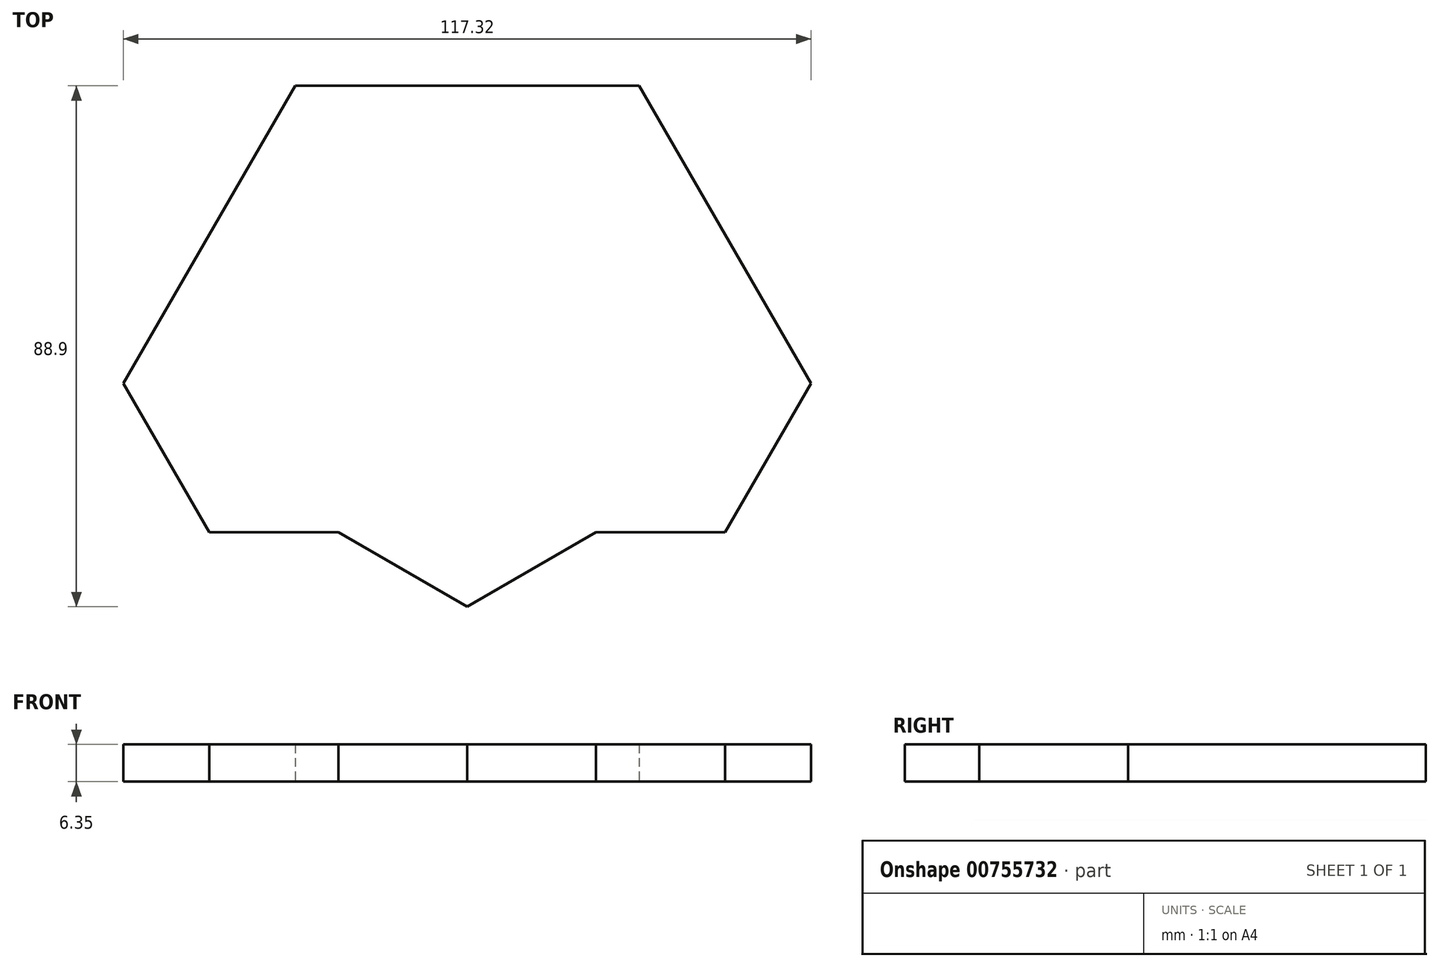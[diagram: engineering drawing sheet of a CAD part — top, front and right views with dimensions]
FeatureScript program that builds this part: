
annotation { "Feature Type Name" : "Feature", "Feature Type Description" : "" }
export const myFeature = defineFeature(function(context is Context, id is Id, definition is map)
    precondition{}
    {
        {
            var Q0;
            Q0=qCreatedBy(makeId("Top.planeOp"),FACE);
            var sketch = newSketch(context, id + "F0", { "sketchPlane" : qUnion([Q0])});
            skLineSegment(sketch, "E0.bottom", {"start": v(-63.5, 50.8) * mm, "end": v(63.5, 50.8) * mm});
            skLineSegment(sketch, "E0.top", {"start": v(-63.5, -50.8) * mm, "end": v(63.5, -50.8) * mm});
            skLineSegment(sketch, "E0.left", {"start": v(-63.5, 50.8) * mm, "end": v(-63.5, -50.8) * mm});
            skLineSegment(sketch, "E0.right", {"start": v(63.5, 50.8) * mm, "end": v(63.5, -50.8) * mm});
            skPoint(sketch, "E0.middle", {"position": v(0, 0) * mm});
            skCircle(sketch, "E1.cCircle", {"center": v(0, 0) * mm, "radius": 50.8 * mm, "construction": true});
            skLineSegment(sketch, "E1.0", {"start": v(-29.33, 50.8) * mm, "end": v(29.33, 50.8) * mm});
            skLineSegment(sketch, "E1.1", {"start": v(29.33, 50.8) * mm, "end": v(58.66, 0) * mm});
            skLineSegment(sketch, "E1.2", {"start": v(58.66, 0) * mm, "end": v(29.33, -50.8) * mm});
            skLineSegment(sketch, "E1.3", {"start": v(29.33, -50.8) * mm, "end": v(-29.33, -50.8) * mm});
            skLineSegment(sketch, "E1.4", {"start": v(-29.33, -50.8) * mm, "end": v(-58.66, 0) * mm});
            skLineSegment(sketch, "E1.5", {"start": v(-58.66, 0) * mm, "end": v(-29.33, 50.8) * mm});
            skPoint(sketch, "E1.0.midPoint", {"position": v(0, 50.8) * mm});
            skLineSegment(sketch, "E2", {"start": v(-44, 25.4) * mm, "end": v(44, 25.4) * mm});
            skLineSegment(sketch, "E3", {"start": v(44, 25.4) * mm, "end": v(44, -25.4) * mm});
            skLineSegment(sketch, "E4", {"start": v(44, -25.4) * mm, "end": v(-44, -25.4) * mm});
            skLineSegment(sketch, "E5", {"start": v(-44, -25.4) * mm, "end": v(-44, 25.4) * mm});
            skLineSegment(sketch, "E6", {"start": v(0, 25.4) * mm, "end": v(0, 50.8) * mm});
            skLineSegment(sketch, "E7", {"start": v(-44, 25.4) * mm, "end": v(0, 25.4) * mm});
            skLineSegment(sketch, "E8", {"start": v(-22, 25.4) * mm, "end": v(0, 38.1) * mm});
            skLineSegment(sketch, "E9", {"start": v(0, 25.4) * mm, "end": v(44, 25.4) * mm});
            skLineSegment(sketch, "E10", {"start": v(22, 25.4) * mm, "end": v(0, 38.1) * mm});
            skLineSegment(sketch, "E11", {"start": v(-44, 0) * mm, "end": v(44, 0) * mm});
            skLineSegment(sketch, "E12.MirrorCS", {"start": v(-22, -25.4) * mm, "end": v(0, -38.1) * mm});
            skLineSegment(sketch, "E13.MirrorCS", {"start": v(22, -25.4) * mm, "end": v(0, -38.1) * mm});
            skSolve(sketch);
        }
        {
            var Q0;
            {var subQ3=sQuery(id+"F0.wireOp",EDGE,"E8");Q0=makeQuery(id+"F0.imprint","IMPRINT",FACE,{"disambiguationData":[TD([[makeQuery(id+"F0.imprint","IMPRINT",EDGE,{"derivedFrom":subQ3}),1.0]])]});}
            var Q1;
            {var subQ3=sQuery(id+"F0.wireOp",EDGE,"E10");Q1=makeQuery(id+"F0.imprint","IMPRINT",FACE,{"disambiguationData":[TD([[makeQuery(id+"F0.imprint","IMPRINT",EDGE,{"derivedFrom":subQ3}),-1.0]])]});}
            var Q2;
            {var subQ0=sQuery(id+"F0.wireOp",EDGE,"E1.2");var subQ1=sQuery(id+"F0.wireOp",EDGE,"E1.1");var subQ2=makeQuery(id+"F0.imprint","INTERSECT",VERTEX,{"derivedFrom":[subQ1,subQ0]});Q2=makeQuery(id+"F0.imprint","IMPRINT",FACE,{"disambiguationData":[TD([[makeQuery(id+"F0.imprint","IMPRINT",EDGE,{"disambiguationData":[TD([[subQ2,1.0]])],"derivedFrom":subQ1}),-1.0]])]});}
            var Q3;
            {var subQ5=sQuery(id+"F0.wireOp",EDGE,"E1.3");Q3=makeQuery(id+"F0.imprint","IMPRINT",FACE,{"disambiguationData":[TD([[makeQuery(id+"F0.imprint","IMPRINT",EDGE,{"derivedFrom":subQ5}),-1.0]])]});}
            var Q4;
            {var subQ0=sQuery(id+"F0.wireOp",EDGE,"E1.5");var subQ1=sQuery(id+"F0.wireOp",EDGE,"E1.4");var subQ2=makeQuery(id+"F0.imprint","INTERSECT",VERTEX,{"derivedFrom":[subQ1,subQ0]});Q4=makeQuery(id+"F0.imprint","IMPRINT",FACE,{"disambiguationData":[TD([[makeQuery(id+"F0.imprint","IMPRINT",EDGE,{"disambiguationData":[TD([[subQ2,1.0]])],"derivedFrom":subQ1}),-1.0]])]});}
            var Q5;
            {var subQ4=sQuery(id+"F0.wireOp",EDGE,"E11");Q5=makeQuery(id+"F0.imprint","IMPRINT",FACE,{"disambiguationData":[TD([[makeQuery(id+"F0.imprint","IMPRINT",EDGE,{"derivedFrom":subQ4}),-1.0]])]});}
            var Q6;
            {var subQ0=sQuery(id+"F0.wireOp",EDGE,"E12.MirrorCS");Q6=makeQuery(id+"F0.imprint","IMPRINT",FACE,{"disambiguationData":[TD([[makeQuery(id+"F0.imprint","IMPRINT",EDGE,{"derivedFrom":subQ0}),1.0]])]});}
            var Q7;
            {var subQ3=sQuery(id+"F0.wireOp",EDGE,"E8");Q7=makeQuery(id+"F0.imprint","IMPRINT",FACE,{"disambiguationData":[TD([[makeQuery(id+"F0.imprint","IMPRINT",EDGE,{"derivedFrom":subQ3}),-1.0]])]});}
            var Q8;
            {var subQ4=sQuery(id+"F0.wireOp",EDGE,"E11");Q8=makeQuery(id+"F0.imprint","IMPRINT",FACE,{"disambiguationData":[TD([[makeQuery(id+"F0.imprint","IMPRINT",EDGE,{"derivedFrom":subQ4}),1.0]])]});}
            var Q9;
            {var subQ3=sQuery(id+"F0.wireOp",EDGE,"E10");Q9=makeQuery(id+"F0.imprint","IMPRINT",FACE,{"disambiguationData":[TD([[makeQuery(id+"F0.imprint","IMPRINT",EDGE,{"derivedFrom":subQ3}),1.0]])]});}
            extrude(context, id + "F1", {"entities" : qUnion([Q0, Q1, Q2, Q3, Q4, Q5, Q6, Q7, Q8, Q9]), "depth" : 6.35 * mm, "offsetDistance" : 25.4 * mm});
        }
    });
